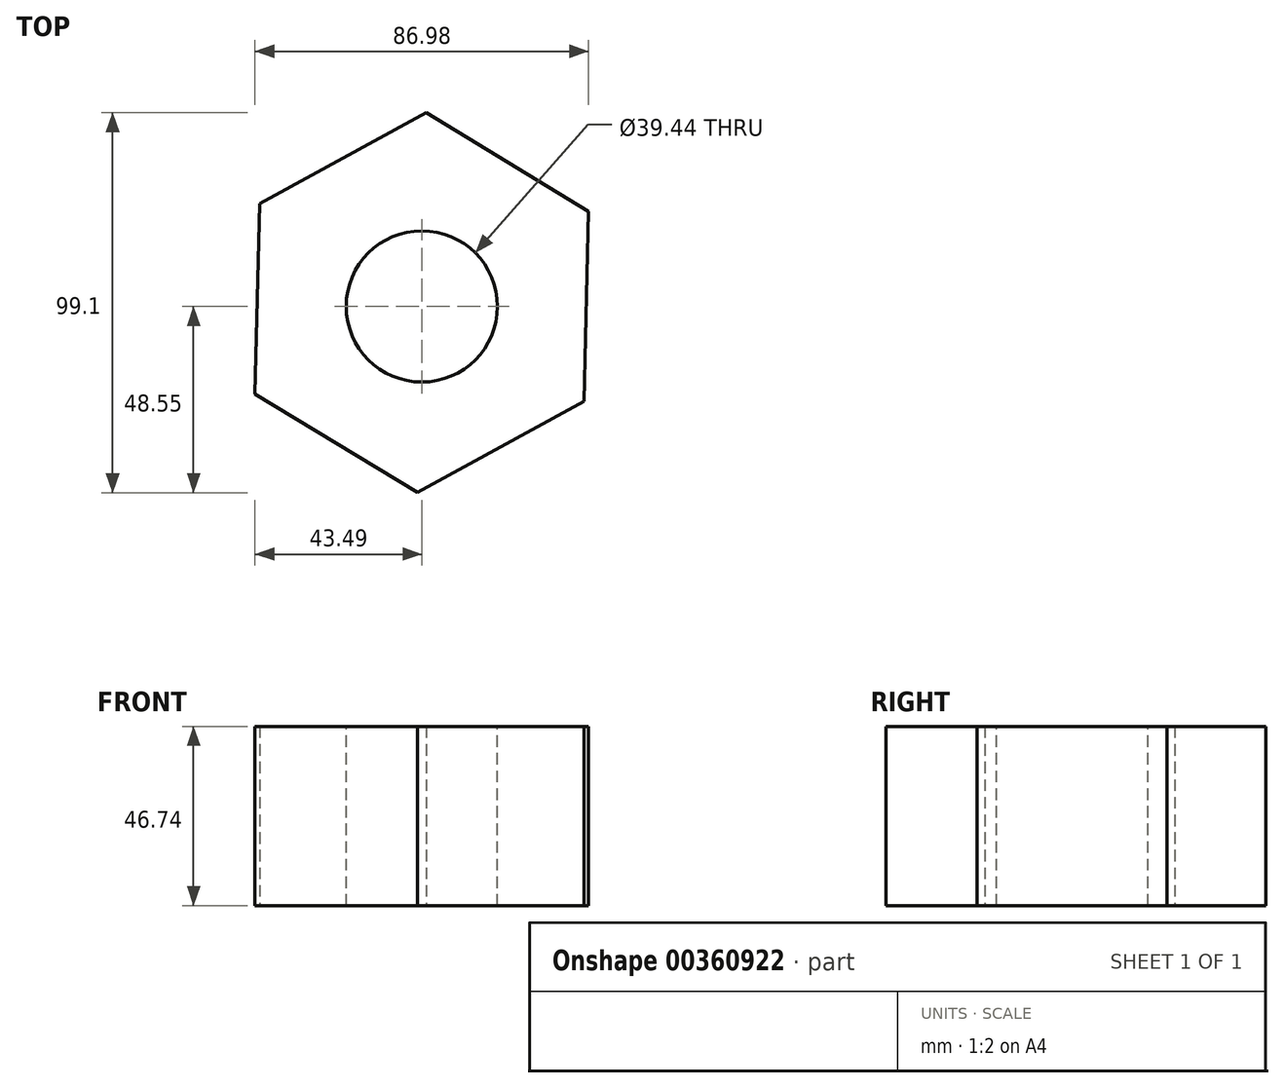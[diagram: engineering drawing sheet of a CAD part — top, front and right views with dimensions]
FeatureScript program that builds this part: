
annotation { "Feature Type Name" : "Feature", "Feature Type Description" : "" }
export const myFeature = defineFeature(function(context is Context, id is Id, definition is map)
    precondition{}
    {
        {
            var Q0;
            Q0=qCreatedBy(makeId("Top.planeOp"),FACE);
            var sketch = newSketch(context, id + "F0", { "sketchPlane" : qUnion([Q0])});
            skCircle(sketch, "E0.cCircle", {"center": v(0, 1) * mm, "radius": 42.92 * mm, "construction": true});
            skLineSegment(sketch, "E0.0", {"start": v(43.49, 24.77) * mm, "end": v(42.33, -24.77) * mm});
            skLineSegment(sketch, "E0.1", {"start": v(42.33, -24.77) * mm, "end": v(-1.15, -48.55) * mm});
            skLineSegment(sketch, "E0.2", {"start": v(-1.15, -48.55) * mm, "end": v(-43.49, -22.77) * mm});
            skLineSegment(sketch, "E0.3", {"start": v(-43.49, -22.77) * mm, "end": v(-42.33, 26.77) * mm});
            skLineSegment(sketch, "E0.4", {"start": v(-42.33, 26.77) * mm, "end": v(1.15, 50.55) * mm});
            skLineSegment(sketch, "E0.5", {"start": v(1.15, 50.55) * mm, "end": v(43.49, 24.77) * mm});
            skPoint(sketch, "E0.0.midPoint", {"position": v(42.9, 0) * mm});
            skSolve(sketch);
        }
        {
            var Q0;
            Q0=makeQuery(id+"F0.imprint","IMPRINT",FACE,{"disambiguationData":[TD([[makeQuery(id+"F0.imprint","IMPRINT",EDGE,{"derivedFrom":sQuery(id+"F0.wireOp",EDGE,"E0.0")}),-1.0]])]});
            extrude(context, id + "F1", {"entities" : qUnion([Q0]), "depth" : 46.74 * mm});
        }
        {
            var Q0;
            Q0=makeQuery(id+"F1.opExtrude","CAP_FACE",FACE,{"disambiguationData":[OSD([sQuery(id+"F0.wireOp",EDGE,"E0.0"),sQuery(id+"F0.wireOp",EDGE,"E0.1"),sQuery(id+"F0.wireOp",EDGE,"E0.2"),sQuery(id+"F0.wireOp",EDGE,"E0.3"),sQuery(id+"F0.wireOp",EDGE,"E0.4"),sQuery(id+"F0.wireOp",EDGE,"E0.5")])],"isStart":false});
            var sketch = newSketch(context, id + "F2", { "sketchPlane" : qUnion([Q0])});
            skCircle(sketch, "E1", {"center": v(0, 0) * mm, "radius": 19.72 * mm});
            skSolve(sketch);
        }
        {
            var Q0;
            Q0=makeQuery(id+"F2.imprint","IMPRINT",FACE,{"disambiguationData":[TD([[makeQuery(id+"F2.imprint","IMPRINT",EDGE,{"derivedFrom":sQuery(id+"F2.wireOp",EDGE,"E1")}),1.0]])]});
            var Q1;
            Q1=makeQuery(id+"F1.opExtrude","CAP_FACE",FACE,{"disambiguationData":[OSD([sQuery(id+"F0.wireOp",EDGE,"E0.0"),sQuery(id+"F0.wireOp",EDGE,"E0.1"),sQuery(id+"F0.wireOp",EDGE,"E0.2"),sQuery(id+"F0.wireOp",EDGE,"E0.3"),sQuery(id+"F0.wireOp",EDGE,"E0.4"),sQuery(id+"F0.wireOp",EDGE,"E0.5")])],"isStart":true});
            extrude(context, id + "F3", {"entities" : qUnion([Q0]), "operationType" : NewBodyOperationType.REMOVE, "endBound" : BoundingType.UP_TO_SURFACE, "oppositeDirection" : true, "endBoundEntityFace" : qUnion([Q1]), "depth" : 25.4 * mm});
        }
    });
